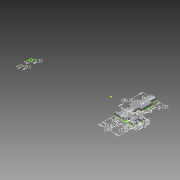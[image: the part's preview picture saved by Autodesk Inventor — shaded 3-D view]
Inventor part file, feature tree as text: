
AUTODESK INVENTOR PART (.ipt)
format: ipt  version: 2013 (Build 170138000, 138)  size: 136,704 bytes
history: native  units: mm
features: other x2, extrude x2, sketch x1
ambient origin geometry x8: Origin, YZ Plane, XZ Plane, XY Plane, X Axis, Y Axis, Z Axis, Center Point
feature tree (5):
  other  "Blocks"
  sketch  "Sketch1"  dims[d0=3.0mm d2=3.0mm d3=0.1mm d7=22.5mm d8=12.4mm d9=4.5mm d10=4.5mm d11=2.0mm d12=2.0mm d32=10.0mm d33=43.25mm d34=3.25mm d35=14.0mm d36=3.25mm d37=3.25mm d38=14.0mm d39=3.25mm d40=3.25mm d41=15.0mm d42=13.0mm d43=3.25mm d44=5.0mm d45=5.0mm d46=3.25mm d47=7.0mm d48=3.25mm d49=12.5mm d50=3.25mm d51=0.0mm d52=3.25mm d53=14.0mm d54=30.25mm d55=8.125mm d56=3.25mm d57=0.0mm d58=2.5mm d59=25.0mm d60=5.5mm]
  extrude  "Extrusion3"  Depth=3.0mm
  extrude  "Extrusion4"  Depth=10.0mm
  other  "Block1"
